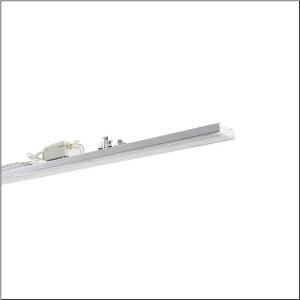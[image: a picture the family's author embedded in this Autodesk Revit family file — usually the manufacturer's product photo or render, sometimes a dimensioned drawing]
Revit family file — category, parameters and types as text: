
# Revit family: licross_11_recessed_mo_51tl18vn465g
name_source: partatom
category: Lighting Fixtures
units: mm (PartAtom-declared; Revit-internal decimal feet)

## family parameters
Cut with Voids When Loaded = No
Host = Face
Light Source = No
Part Type = Normal
Room Calculation Point = No
Round Connector Dimension = Use Diameter
Shared = No

## types (1)
- --- (1 x LED, 6520 lm, 36 W, 4000K)
    Apparent Load = 36 VA
    CIE Flux Codes = 83 96 99 100 100
    Color Rendering = 80
    Color Temperature = 4000K
    Default Elevation = 1800 mm
    Description = Licross 11 Recessed MO, luminaire insert, of sheet steel, galvanised, coil coated, white, length: 1.500mm, width: 66mm, height: 67mm, LED rated luminous flux: 6.520lm, light colour: 840, SDCM (Standard Deviation of Colour Matching)MacAdam ≤ 2 SDCM (initial), control gear: DALI 2, CLO, with plug, 5-pole, with phase selection, mains connection: 220..240V, AC, 50/60Hz, start of lifetime: 36W, end of service life: 41W, internal wiring halogen-free, primary optical cover: cover, of PMMA, light emission: direct distribution, primary light characteristic: symmetric, protection rating (complete): IP40, insulation class (complete): insulation class I (protective earthing), certification: CE, ENEC, VDE, UKCA, protection symbol: D if used in an environment without relevant dust loads with corresponding accessories, impact resistance: IK06, permissible ambient temperature for indoor applications: -25..+40°C, corresponds to IFS (International Featured Standards) requirements for safety and quality in the food industry, reducing of maximum allowable ambient temperature of 5°C with ceiling mounting, LABS conformity tested according to VDMA 24364:2018-05, The light source and the operating device comply with the requirements of the Ecodesign Regulation (EU) 2019/2020 and are replaceable in accordance with this regulation, packaging unit: 1 piece
    Height = 58 mm
    Lamp = 1 x LED
    Lamp Light Flux = 6520 lm
    Lamp Power = 36 W
    Lamp count = 1
    Length = 1500 mm
    Luminous efficacy = 181 lm/W
    Manufacturer = Siteco
    ModVariant = No
    Model = 51TL18VN465G
    Mounting Place = Ceiling
    Mounting Type = Pendant
    Number of Poles = 1
    OnlyDefault = Yes
    Power Factor = 1
    Product Name = Licross 11 Recessed MO
    Product group = luminaire insert | ceiling pendant
    ProductGroupID = 901
    Protection Class = Protection class I
    Protection Degree = IP 40
    RLX_Detail_Level = 1
    RLX_Emergency_Light_Flux = 0 lm
    RLX_Emergency_Type = 0
    RLX_Emergency_Type_DB = No
    RlxData = <blob elided: 24757 chars, md5=37be76ab>
    Socket = socket
    Standby Power = 0 W
    System Light Flux = 6520 lm
    System Power = 36 W
    Type Comments = factory setting: luminous flux: 100 % | dim-lin: 254 | 240 mA
    Type Image = l_1296930.jpg
    URL = http://relux.com
    VarID = @adj_000177
    Voltage = 0 V
    Weight = 0.00 kg
    Width = 66 mm

## geometry (parser evidence)
native form markers: Blend x4, Sweep x13
no freeform markers — native parametric forms only
